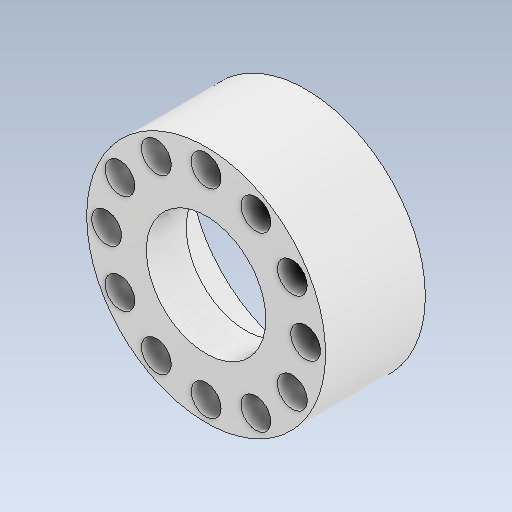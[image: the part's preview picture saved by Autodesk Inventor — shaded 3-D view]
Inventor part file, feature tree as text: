
AUTODESK INVENTOR PART (.ipt)
format: ipt  version: 2023 (Build 270158000, 158)  size: 162,304 bytes
history: native  units: in
note: dims shown in document units (in); Inventor stores cm internally (conversion verified against a paired STEP export)
features: other x3, sketch x1
ambient origin geometry x8: Origin, YZ Plane, XZ Plane, XY Plane, X Axis, Y Axis, Z Axis, Center Point
bodies: Solid1 (feature_tree)
feature tree (4):
  other  "HubCap_v7.ipt"
  other  "Solid1::HubCap_v7.ipt"
  other  "TaggingFeature1"
  sketch  "Sketch1"  dims[d0=0.3937in]
